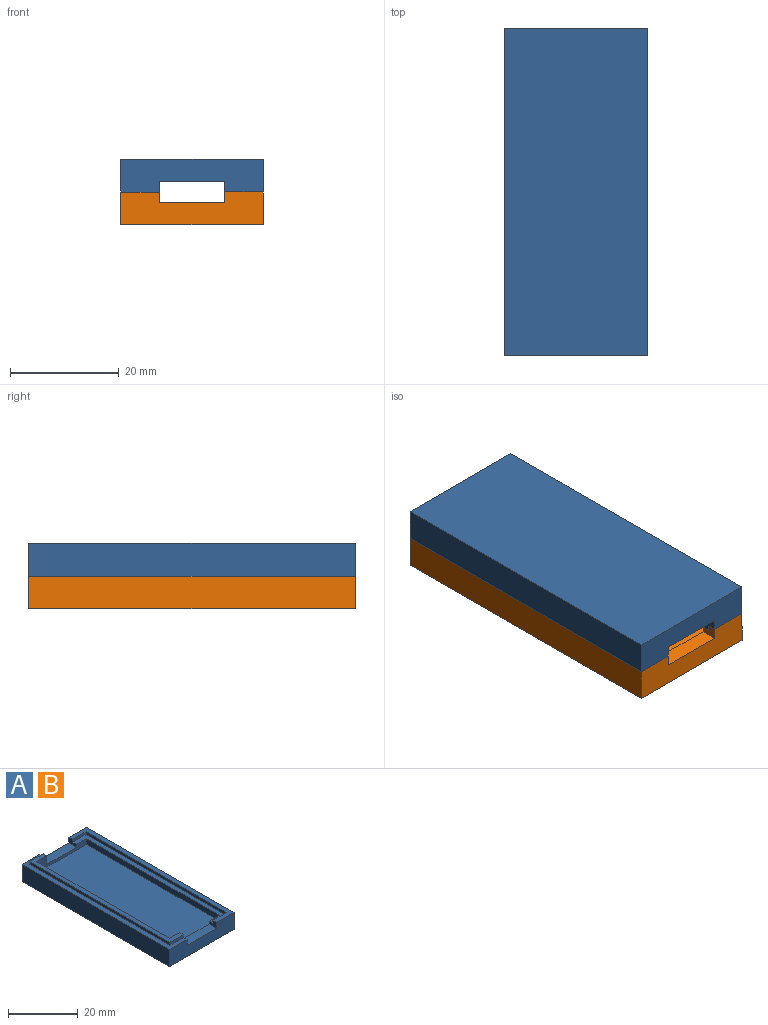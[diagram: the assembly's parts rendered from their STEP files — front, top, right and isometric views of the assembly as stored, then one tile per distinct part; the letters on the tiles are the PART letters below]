
ASSEMBLY  parts=2 mates=1
PART A: 26 faces, bbox 26.2x60x7 mm
  f0: plane 3x2mm, normal (-1,0,0), area 4.5mm2, adj f1,f5,f8,f14,f23,f25
  f1: plane 20.2x4mm, normal (0,-1,0), area 36.6mm2, adj f0,f3,f11,f12,f13,f14,f21,f25
  f2: plane 20.2x4mm, normal (0,1,0), area 36.6mm2, adj f3,f11,f12,f15,f16,f17,f21,f25
  f3: plane 54x2mm, normal (-1,0,0), area 108mm2, adj f1,f2,f12,f25
  f4: plane 60x7.1mm, normal (0,0,1), area 115.6mm2, adj f6,f8,f9,f13,f15,f18,f19,f20
  f5: plane 60x7.1mm, normal (0,0,1), area 115.6mm2, adj f0,f6,f7,f8,f16,f22,f23,f24
  f6: plane 26.2x6mm, normal (0,-1,0), area 133.2mm2, adj f4,f5,f7,f9,f10,f15,f16,f17
  f7: plane 60x6mm, normal (1,0,0), area 360mm2, adj f5,f6,f8,f10
  f8: plane 26.2x6mm, normal (0,1,0), area 133.2mm2, adj f0,f4,f5,f7,f9,f10,f13,f14
  f9: plane 60x6mm, normal (-1,0,0), area 360mm2, adj f4,f6,f8,f10
  f10: plane 60x26.2mm, normal (0,0,-1), area 1572mm2, adj f6,f7,f8,f9
  f11: plane 54x4mm, normal (1,0,0), area 216mm2, adj f1,f2,f12,f21
  f12: plane 54x20.2mm, normal (0,0,1), area 1090.8mm2, adj f1,f2,f3,f11
  f13: plane 3x3mm, normal (1,0,0), area 7.5mm2, adj f1,f4,f8,f14,f20,f21
  f14: plane 12x3mm, normal (0,0,1), area 36mm2, adj f0,f1,f8,f13
  f15: plane 3x3mm, normal (1,0,0), area 7.5mm2, adj f2,f4,f6,f17,f19,f21
  f16: plane 3x2mm, normal (-1,0,0), area 4.5mm2, adj f2,f5,f6,f17,f24,f25
  f17: plane 12x3mm, normal (0,0,1), area 36mm2, adj f2,f6,f15,f16
  f18: plane 57x1mm, normal (-1,0,0), area 57mm2, adj f4,f19,f20,f21
  f19: plane 5.45x1mm, normal (0,-1,0), area 5.4mm2, adj f4,f15,f18,f21
  f20: plane 5.45x1mm, normal (0,1,0), area 5.4mm2, adj f4,f13,f18,f21
  f21: plane 57x5.45mm, normal (0,0,1), area 89mm2, adj f1,f2,f11,f13,f15,f18,f19,f20
  f22: plane 57x1mm, normal (-1,0,0), area 57mm2, adj f5,f23,f24,f25
  f23: plane 5.45x1mm, normal (0,-1,0), area 5.4mm2, adj f0,f5,f22,f25
  f24: plane 5.45x1mm, normal (0,1,0), area 5.4mm2, adj f5,f16,f22,f25
  f25: plane 57x5.45mm, normal (0,0,1), area 89mm2, adj f0,f1,f2,f3,f16,f22,f23,f24
PART B: same geometry as A
PLACE A rot(axis=(0,1,0),180deg) t=(-13.36,4.98,21.41)mm
PLACE B t=(-13.36,4.98,9.41)mm
MATE fastened B.f5 <-> A.f4  axis (0,0,1) through (-0.26,-25.02,15.41)mm
